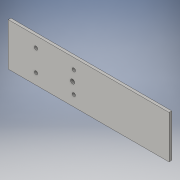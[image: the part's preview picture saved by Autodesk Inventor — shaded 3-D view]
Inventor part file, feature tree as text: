
AUTODESK INVENTOR PART (.ipt)
format: ipt  version: 2016 (Build 200138000, 138)  size: 97,280 bytes
history: native  units: in
note: dims shown in document units (in); Inventor stores cm internally (conversion verified against a paired STEP export)
features: extrude x1, sketch x1
ambient origin geometry x8: Origin, YZ Plane, XZ Plane, XY Plane, X Axis, Y Axis, Z Axis, Center Point
bodies: Solid1 (feature_tree)
feature tree (2):
  extrude  "Extrusion1"  Depth=0.125in
  sketch  "Sketch1"  dims[d0=4.5in d1=1.0in d2=1.0in d3=7.5in d4=0.125in d5=0.0in d6=1.765in]
